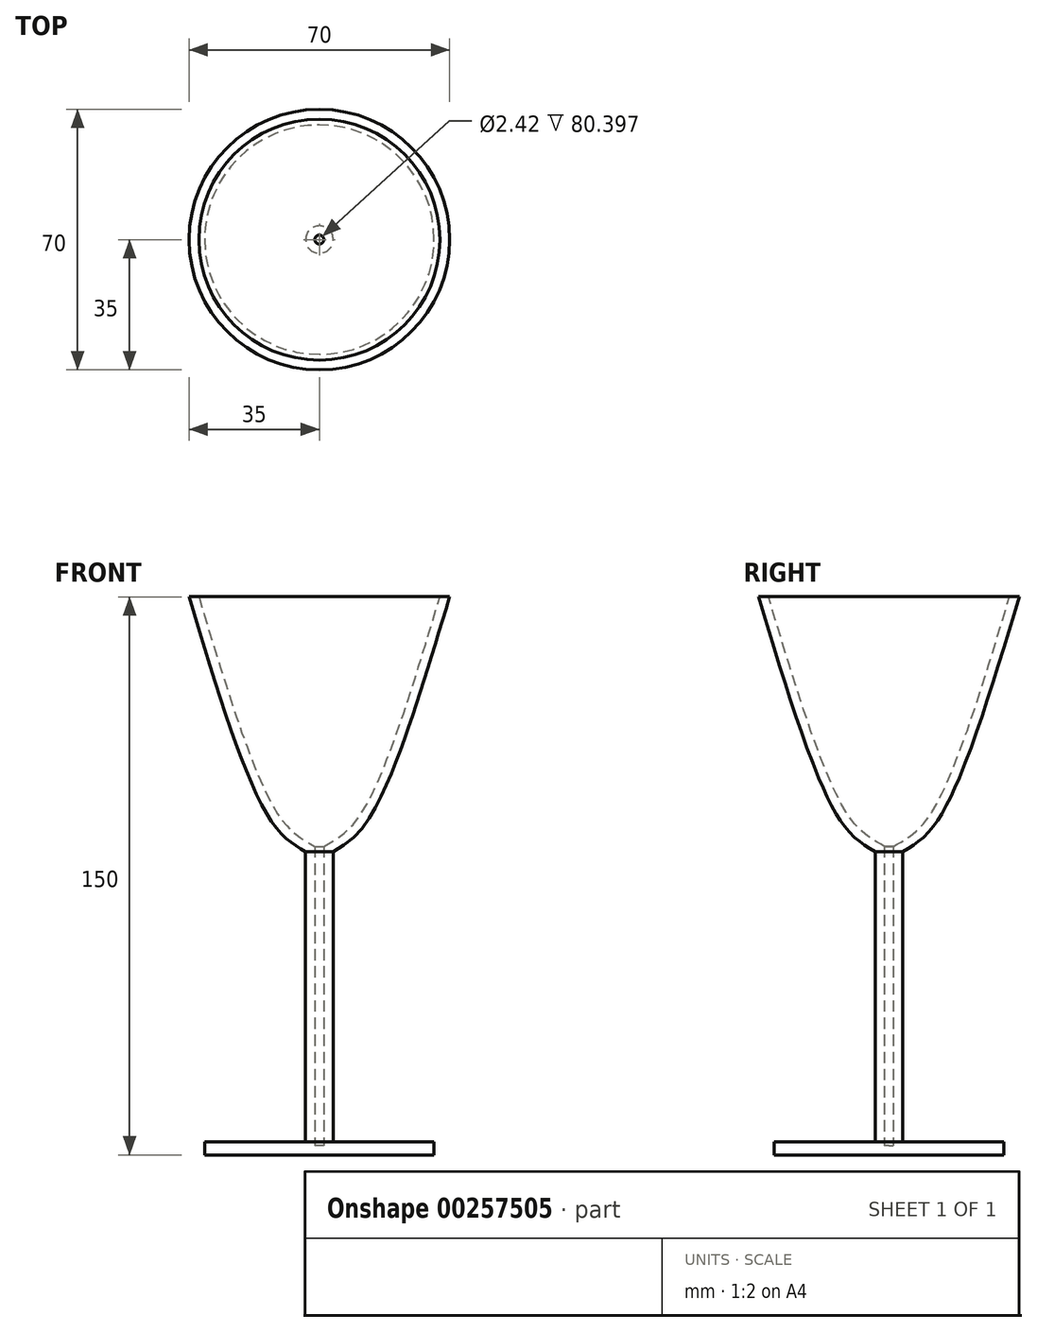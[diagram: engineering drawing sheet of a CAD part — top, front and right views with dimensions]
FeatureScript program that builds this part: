
annotation { "Feature Type Name" : "Feature", "Feature Type Description" : "" }
export const myFeature = defineFeature(function(context is Context, id is Id, definition is map)
    precondition{}
    {
        {
            var Q0;
            Q0=qCreatedBy(makeId("Front.planeOp"),FACE);
            var sketch = newSketch(context, id + "F0", { "sketchPlane" : qUnion([Q0])});
            skLineSegment(sketch, "E0.top", {"start": v(0, 74.65) * mm, "end": v(35, 74.65) * mm});
            skLineSegment(sketch, "E0.left", {"start": v(0, -75.35) * mm, "end": v(0, 74.65) * mm});
            skFitSpline(sketch, "E1", {"points": [v(35, 74.65) * mm, v(12.89, 14.3) * mm, v(3.71, 6.13) * mm], "startDerivative": vector(-32.35, -107.56) * mm, "endDerivative": vector(-29.92, -17.78) * mm});
            skLineSegment(sketch, "E2", {"start": v(3.71, 6.13) * mm, "end": v(3.71, -71.89) * mm});
            skLineSegment(sketch, "E3", {"start": v(3.71, -71.89) * mm, "end": v(30.85, -71.89) * mm});
            skLineSegment(sketch, "E4", {"start": v(30.85, -71.89) * mm, "end": v(30.85, -75.35) * mm});
            skLineSegment(sketch, "E5", {"start": v(30.85, -75.35) * mm, "end": v(3.71, -75.35) * mm});
            skLineSegment(sketch, "E6", {"start": v(3.71, -75.35) * mm, "end": v(0, -75.35) * mm});
            skSolve(sketch);
        }
        {
            var Q0;
            Q0=makeQuery(id+"F0.imprint","IMPRINT",FACE,{"disambiguationData":[TD([[makeQuery(id+"F0.imprint","IMPRINT",EDGE,{"derivedFrom":sQuery(id+"F0.wireOp",EDGE,"E0.top")}),-1.0]])]});
            var Q1;
            Q1=sQuery(id+"F0.wireOp",EDGE,"E0.left");
            revolve(context, id + "F1", {"entities" : qUnion([Q0]), "axis" : qUnion([Q1]), "revolveType" : RevolveType.FULL});
        }
        {
            var Q0;
            Q0=makeQuery(id+"F1.opRevolve","SWEPT_FACE",FACE,{"disambiguationData":[OSD([sQuery(id+"F0.wireOp",EDGE,"E0.top")])]});
            shell(context, id + "F2", {"entities" : qUnion([Q0]), "thickness" : 2.5 * mm});
        }
    });
